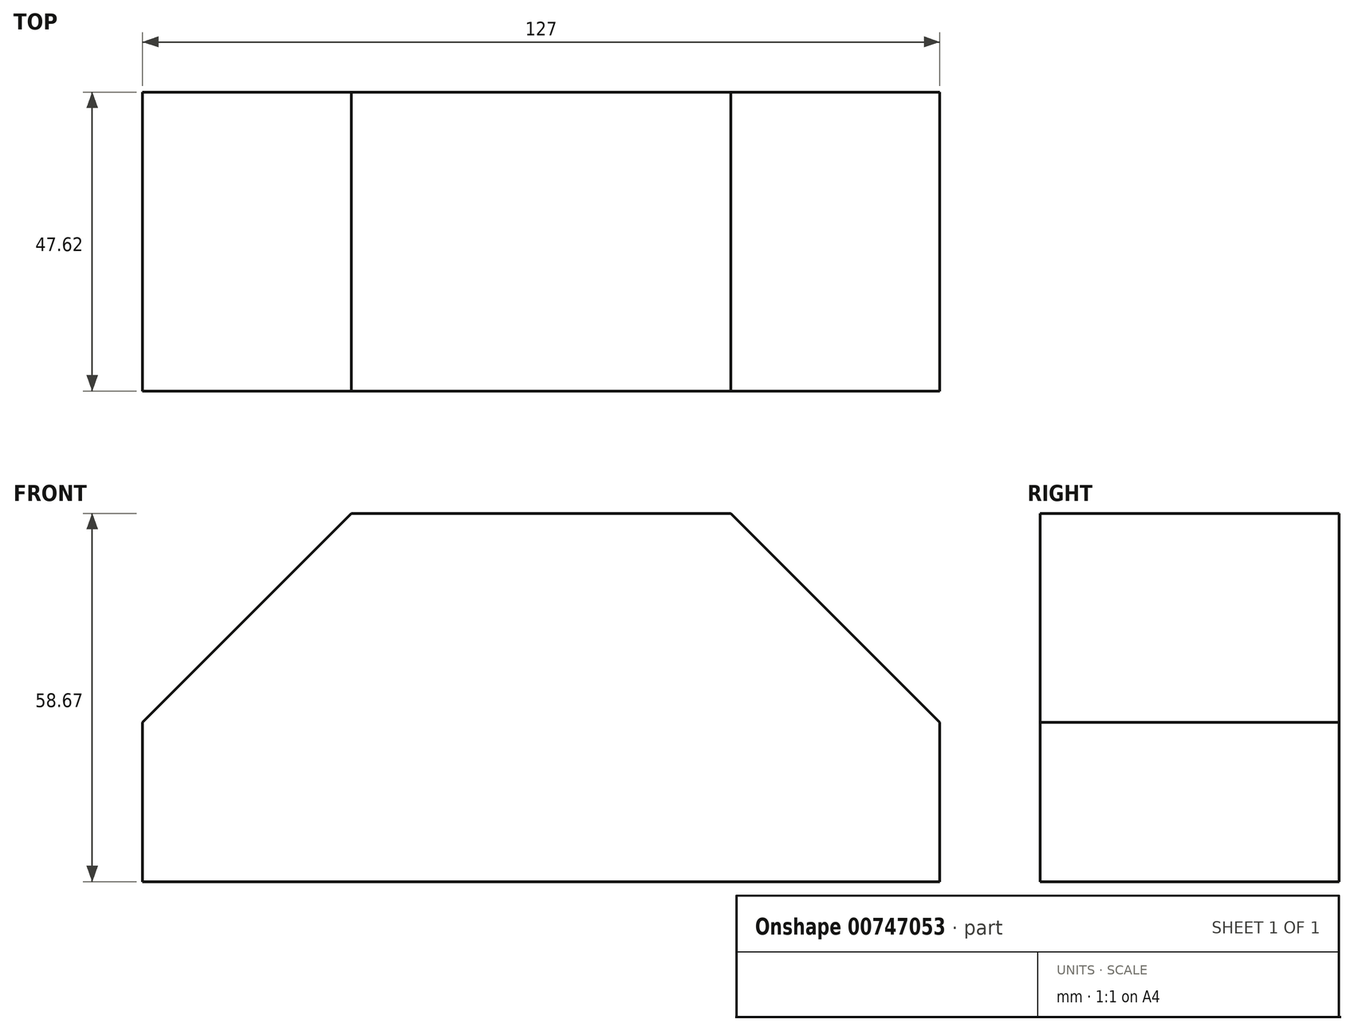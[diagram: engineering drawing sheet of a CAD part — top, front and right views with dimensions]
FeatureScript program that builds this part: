
annotation { "Feature Type Name" : "Feature", "Feature Type Description" : "" }
export const myFeature = defineFeature(function(context is Context, id is Id, definition is map)
    precondition{}
    {
        {
            var Q0;
            Q0=qCreatedBy(makeId("Front.planeOp"),FACE);
            var sketch = newSketch(context, id + "F0", { "sketchPlane" : qUnion([Q0])});
            skLineSegment(sketch, "E0", {"start": v(-66.4, 0) * mm, "end": v(-33.13, 33.27) * mm});
            skLineSegment(sketch, "E1", {"start": v(-33.13, 33.27) * mm, "end": v(27.32, 33.27) * mm});
            skLineSegment(sketch, "E2", {"start": v(27.32, 33.27) * mm, "end": v(60.6, 0) * mm});
            skLineSegment(sketch, "E3", {"start": v(60.6, 0) * mm, "end": v(60.6, -25.4) * mm});
            skLineSegment(sketch, "E4", {"start": v(60.6, -25.4) * mm, "end": v(-66.4, -25.4) * mm});
            skLineSegment(sketch, "E5", {"start": v(-66.4, -25.4) * mm, "end": v(-66.4, 0) * mm});
            skSolve(sketch);
        }
        {
            var Q0;
            Q0=makeQuery(id+"F0.imprint","IMPRINT",FACE,{"disambiguationData":[TD([[makeQuery(id+"F0.imprint","IMPRINT",EDGE,{"derivedFrom":sQuery(id+"F0.wireOp",EDGE,"E0")}),-1.0]])]});
            extrude(context, id + "F1", {"entities" : qUnion([Q0]), "depth" : 47.62 * mm, "offsetDistance" : 25.4 * mm});
        }
    });
